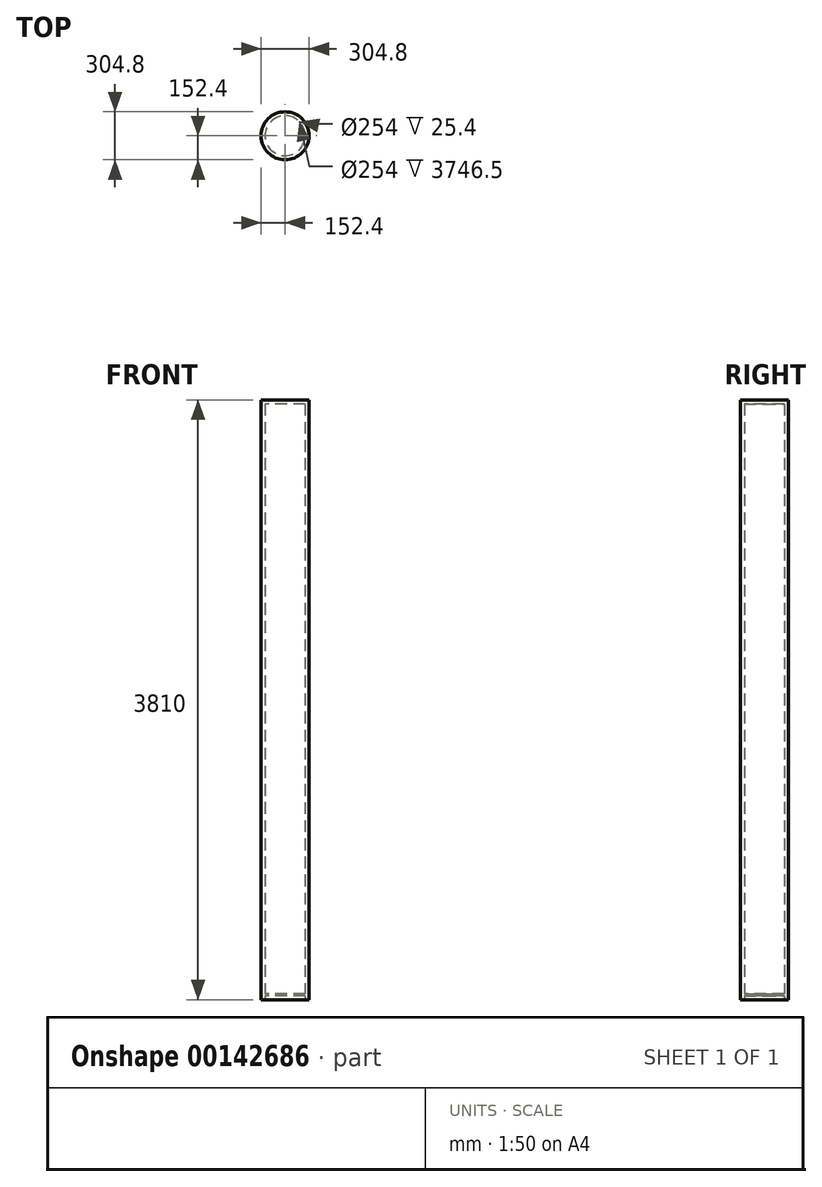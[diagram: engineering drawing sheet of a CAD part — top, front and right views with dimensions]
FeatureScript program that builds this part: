
annotation { "Feature Type Name" : "Feature", "Feature Type Description" : "" }
export const myFeature = defineFeature(function(context is Context, id is Id, definition is map)
    precondition{}
    {
        {
            var Q0;
            Q0=qCreatedBy(makeId("Top.planeOp"),FACE);
            var sketch = newSketch(context, id + "F0", { "sketchPlane" : qUnion([Q0])});
            skCircle(sketch, "E0", {"center": v(0, 0) * mm, "radius": 152.4 * mm});
            skSolve(sketch);
        }
        {
            var Q0;
            Q0 = qSketchRegion(id + "F0", true);
            extrude(context, id + "F1", {"entities" : qUnion([Q0]), "depth" : 3810 * mm});
        }
        {
            var Q0;
            Q0=makeQuery(id+"F1.opExtrude","CAP_FACE",FACE,{"disambiguationData":[OSD([sQuery(id+"F0.wireOp",EDGE,"E0")])],"isStart":true});
            var Q1;
            Q1=makeQuery(id+"F1.opExtrude","SWEPT_BODY",BODY,{"disambiguationData":[OSD([sQuery(id+"F0.wireOp",EDGE,"E0")])]});
            shell(context, id + "F2", {"entities" : qUnion([Q0]), "parts" : qUnion([Q1]), "thickness" : 25.4 * mm});
        }
        {
            var Q0;
            Q0=qCreatedBy(makeId("Top.planeOp"),FACE);
            cPlane(context, id + "F3", {"entities" : qUnion([Q0]), "cplaneType" : CPlaneType.OFFSET, "offset" : 25.4 * mm, "width" : 152.4 * mm, "height" : 152.4 * mm});
        }
        {
            var Q0;
            Q0=qCreatedBy(id+"F3.planeOp",FACE);
            var sketch = newSketch(context, id + "F4", { "sketchPlane" : qUnion([Q0])});
            skCircle(sketch, "E1", {"center": v(0, 0) * mm, "radius": 142.29 * mm});
            skSolve(sketch);
        }
        {
            var Q0;
            Q0=makeQuery(id+"F4.imprint","IMPRINT",FACE,{"disambiguationData":[TD([[makeQuery(id+"F4.imprint","IMPRINT",EDGE,{"derivedFrom":sQuery(id+"F4.wireOp",EDGE,"E1")}),1.0]])]});
            extrude(context, id + "F5", {"entities" : qUnion([Q0]), "operationType" : NewBodyOperationType.ADD, "depth" : 12.7 * mm});
        }
    });
